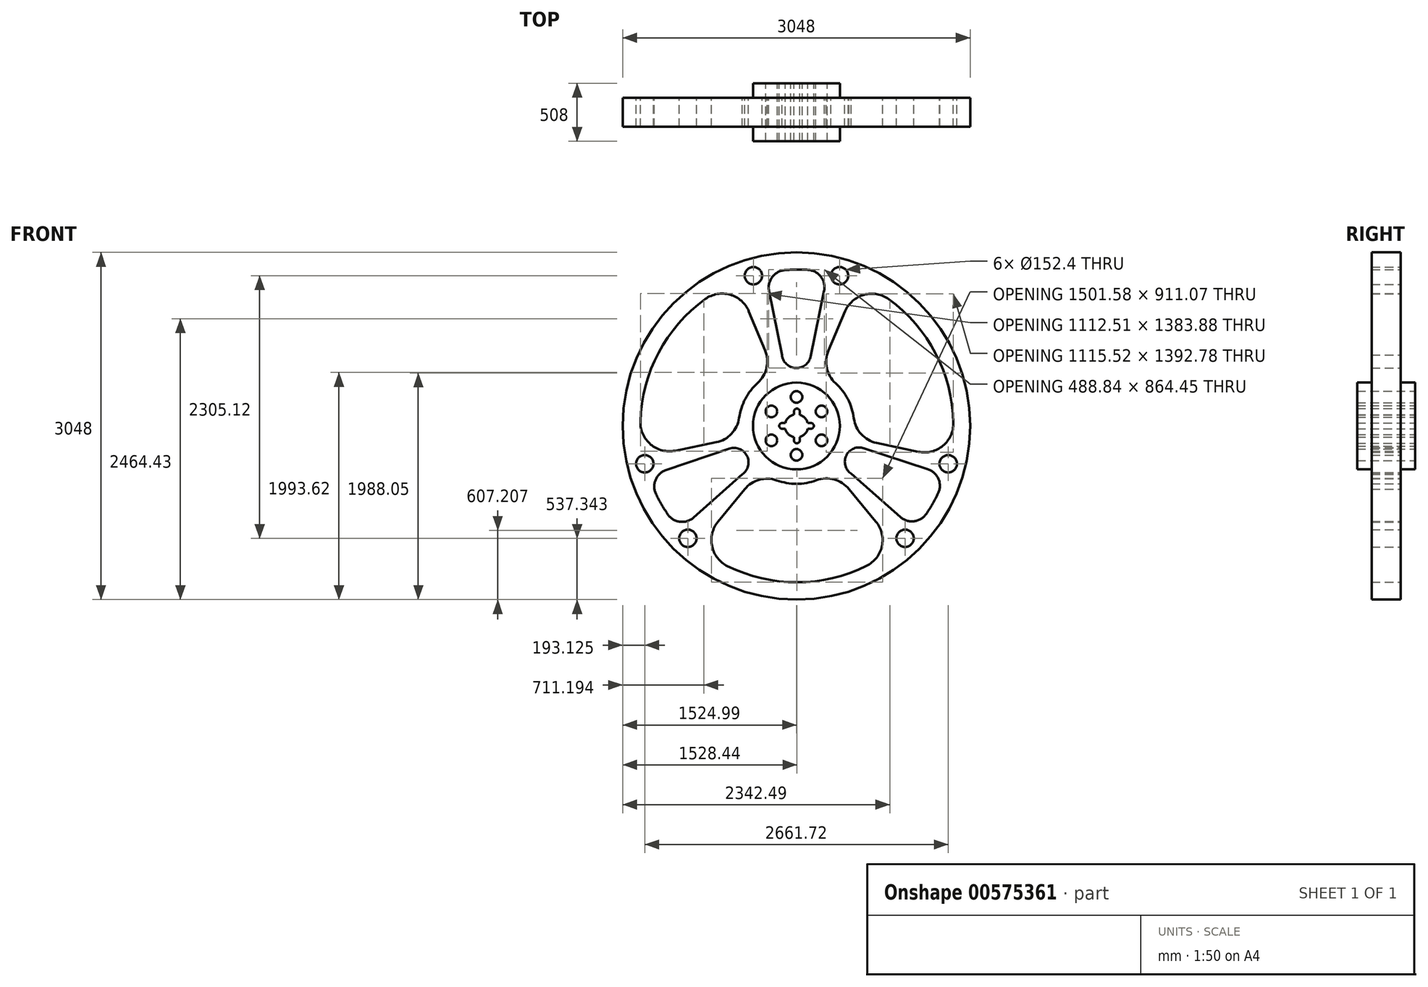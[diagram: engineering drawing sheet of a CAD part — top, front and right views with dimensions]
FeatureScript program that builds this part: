
annotation { "Feature Type Name" : "Feature", "Feature Type Description" : "" }
export const myFeature = defineFeature(function(context is Context, id is Id, definition is map)
    precondition{}
    {
        {
            var Q0;
            Q0=qCreatedBy(makeId("Front.planeOp"),FACE);
            var sketch = newSketch(context, id + "F0", { "sketchPlane" : qUnion([Q0])});
            skCircle(sketch, "E0", {"center": v(0, 0) * mm, "radius": 1524 * mm});
            skArc(sketch, "E1", {"start": v(503.66, 66.28) * mm, "mid": v(450.5, 234.77) * mm, "end": v(342.84, 374.86) * mm});
            skCircle(sketch, "E2", {"center": v(-378.06, 1318.47) * mm, "radius": 76.2 * mm});
            skCircle(sketch, "E3", {"center": v(378.06, 1318.47) * mm, "radius": 76.2 * mm});
            skCircle(sketch, "E4.1.0", {"center": v(-952.81, -986.64) * mm, "radius": 76.2 * mm});
            skCircle(sketch, "E4.1.1", {"center": v(-1330.88, -331.8) * mm, "radius": 76.2 * mm});
            skCircle(sketch, "E4.2.0", {"center": v(1330.84, -331.83) * mm, "radius": 76.2 * mm});
            skCircle(sketch, "E4.2.1", {"center": v(952.78, -986.66) * mm, "radius": 76.2 * mm});
            skPoint(sketch, "E4.center", {"position": v(-0.01, 0) * mm});
            skLineSegment(sketch, "E5", {"start": v(-588.68, -199.42) * mm, "end": v(-1143.8, -387.47) * mm});
            skLineSegment(sketch, "E6", {"start": v(-451.96, -402.88) * mm, "end": v(-901.6, -803.7) * mm});
            skLineSegment(sketch, "E7", {"start": v(457.22, -400.88) * mm, "end": v(912.5, -800.05) * mm});
            skLineSegment(sketch, "E8", {"start": v(590.9, -194.77) * mm, "end": v(1152.91, -380.02) * mm});
            skLineSegment(sketch, "E9", {"start": v(702.79, -149.05) * mm, "end": v(1069.6, -226.85) * mm});
            skLineSegment(sketch, "E10", {"start": v(460.78, -555.07) * mm, "end": v(696.7, -839.27) * mm});
            skLineSegment(sketch, "E11", {"start": v(-455.06, -555.92) * mm, "end": v(-688.92, -841.6) * mm});
            skLineSegment(sketch, "E12", {"start": v(-240.4, 1185.5) * mm, "end": v(-120.85, 595.95) * mm});
            skLineSegment(sketch, "E13", {"start": v(242.35, 1187.25) * mm, "end": v(124.43, 609.6) * mm});
            skLineSegment(sketch, "E14", {"start": v(426.43, 1005.85) * mm, "end": v(280.41, 661.44) * mm});
            skLineSegment(sketch, "E15", {"start": v(-275.36, 663.56) * mm, "end": v(-417.14, 1005.24) * mm});
            skLineSegment(sketch, "E16", {"start": v(-703.9, -143.68) * mm, "end": v(-1064.36, -217.26) * mm});
            skArc(sketch, "E17.trimOffspring", {"start": v(-173.09, -477.6) * mm, "mid": v(0.96, -508) * mm, "end": v(174.88, -476.95) * mm});
            skArc(sketch, "E18.trimOffspring", {"start": v(-339.97, 377.47) * mm, "mid": v(-448.7, 238.2) * mm, "end": v(-503.14, 70.12) * mm});
            skArc(sketch, "E19.trimOffspring", {"start": v(-800.46, 1113.8) * mm, "mid": v(-1210.3, 642.6) * mm, "end": v(-1369.06, 38.62) * mm});
            skArc(sketch, "E20.trimOffspring", {"start": v(102.94, 1369.8) * mm, "mid": v(-0.64, 1372.63) * mm, "end": v(-104.13, 1367.63) * mm});
            skArc(sketch, "E21.trimOffspring", {"start": v(1376.26, 26.37) * mm, "mid": v(1220.64, 636.09) * mm, "end": v(809.37, 1112.36) * mm});
            skArc(sketch, "E22.trimOffspring", {"start": v(1139.02, -771.13) * mm, "mid": v(1194.32, -682.72) * mm, "end": v(1242.76, -590.36) * mm});
            skArc(sketch, "E23.trimOffspring", {"start": v(-604.91, -1230.2) * mm, "mid": v(4.81, -1372.33) * mm, "end": v(614.25, -1228.99) * mm});
            skArc(sketch, "E24.trimOffspring", {"start": v(-1232.03, -598.3) * mm, "mid": v(-1183.69, -689.17) * mm, "end": v(-1128.67, -776.16) * mm});
            skArc(sketch, "E25", {"start": v(-126.51, 623.9) * mm, "mid": v(-7.22, 508.2) * mm, "end": v(124.43, 609.6) * mm});
            skArc(sketch, "E26", {"start": v(590.9, -194.77) * mm, "mid": v(437.5, -258.68) * mm, "end": v(478.67, -419.68) * mm});
            skArc(sketch, "E27", {"start": v(-476.28, -424.56) * mm, "mid": v(-434.3, -262.98) * mm, "end": v(-588.68, -199.42) * mm});
            skArc(sketch, "E28", {"start": v(-688.92, -841.6) * mm, "mid": v(-740.64, -1056.15) * mm, "end": v(-604.91, -1230.2) * mm});
            skArc(sketch, "E29", {"start": v(614.25, -1228.99) * mm, "mid": v(749.76, -1054.08) * mm, "end": v(696.7, -839.27) * mm});
            skArc(sketch, "E30.trimOffspring", {"start": v(-173.09, -477.6) * mm, "mid": v(-326.49, -472.07) * mm, "end": v(-455.06, -555.92) * mm});
            skArc(sketch, "E31.trimOffspring", {"start": v(460.78, -555.07) * mm, "mid": v(330.4, -469.99) * mm, "end": v(174.88, -476.95) * mm});
            skArc(sketch, "E32", {"start": v(-1369.06, 38.62) * mm, "mid": v(-1278.5, -162.9) * mm, "end": v(-1064.36, -217.26) * mm});
            skArc(sketch, "E33", {"start": v(-417.14, 1005.24) * mm, "mid": v(-582.53, 1152.27) * mm, "end": v(-800.46, 1113.8) * mm});
            skArc(sketch, "E34", {"start": v(-339.97, 377.47) * mm, "mid": v(-262.2, 510.24) * mm, "end": v(-275.36, 663.56) * mm});
            skArc(sketch, "E35", {"start": v(280.41, 661.44) * mm, "mid": v(266.09, 508.23) * mm, "end": v(342.84, 374.86) * mm});
            skArc(sketch, "E36", {"start": v(809.37, 1112.36) * mm, "mid": v(592.22, 1151.42) * mm, "end": v(426.43, 1005.85) * mm});
            skArc(sketch, "E37", {"start": v(503.66, 66.28) * mm, "mid": v(569, -73.03) * mm, "end": v(702.79, -149.05) * mm});
            skArc(sketch, "E38", {"start": v(-703.9, -143.68) * mm, "mid": v(-569.54, -68.69) * mm, "end": v(-503.14, 70.12) * mm});
            skArc(sketch, "E39", {"start": v(1069.6, -226.85) * mm, "mid": v(1284.03, -174.23) * mm, "end": v(1376.26, 26.37) * mm});
            skArc(sketch, "E40", {"start": v(-104.13, 1367.63) * mm, "mid": v(-213.06, 1307.1) * mm, "end": v(-240.4, 1185.5) * mm});
            skArc(sketch, "E41", {"start": v(242.35, 1187.25) * mm, "mid": v(214.15, 1310.22) * mm, "end": v(102.94, 1369.8) * mm});
            skArc(sketch, "E42", {"start": v(-1143.8, -387.47) * mm, "mid": v(-1235.48, -472.97) * mm, "end": v(-1232.03, -598.3) * mm});
            skArc(sketch, "E43", {"start": v(-1128.67, -776.16) * mm, "mid": v(-1021.36, -841.22) * mm, "end": v(-901.6, -803.7) * mm});
            skArc(sketch, "E44", {"start": v(912.5, -800.05) * mm, "mid": v(1032.28, -836.63) * mm, "end": v(1139.02, -771.13) * mm});
            skArc(sketch, "E45", {"start": v(1242.76, -590.36) * mm, "mid": v(1245.35, -464.9) * mm, "end": v(1152.91, -380.02) * mm});
            skCircle(sketch, "E46", {"center": v(0, 0) * mm, "radius": 381 * mm});
            skArc(sketch, "E47", {"start": v(3.46, -152.36) * mm, "mid": v(4.15, -152.34) * mm, "end": v(4.84, -152.32) * mm});
            skArc(sketch, "E48", {"start": v(98.2, 26.04) * mm, "mid": v(72.86, 70.8) * mm, "end": v(28.86, 97.41) * mm});
            skLineSegment(sketch, "E49", {"start": v(-152.4, 0) * mm, "end": v(-151.18, 0) * mm});
            skCircle(sketch, "E50", {"center": v(0, 254) * mm, "radius": 50.8 * mm});
            skCircle(sketch, "E51.1.0", {"center": v(-219.97, 127) * mm, "radius": 50.8 * mm});
            skCircle(sketch, "E51.2.0", {"center": v(-219.97, -127) * mm, "radius": 50.8 * mm});
            skCircle(sketch, "E51.3.0", {"center": v(0, -254) * mm, "radius": 50.8 * mm});
            skCircle(sketch, "E51.4.0", {"center": v(219.97, -127) * mm, "radius": 50.8 * mm});
            skCircle(sketch, "E51.5.0", {"center": v(219.97, 127) * mm, "radius": 50.8 * mm});
            skPoint(sketch, "E52.orphan", {"position": v(-381, 0) * mm});
            skLineSegment(sketch, "E53.trimOffspring", {"start": v(0, 254) * mm, "end": v(0, 381) * mm});
            skLineSegment(sketch, "E54.trimOffspring", {"start": v(-101.61, 0) * mm, "end": v(-100.38, 0) * mm});
            skPoint(sketch, "E55.start.orphan", {"position": v(0, -381) * mm});
            skArc(sketch, "E56", {"start": v(127, -24.76) * mm, "mid": v(152.4, 0.64) * mm, "end": v(127, 26.04) * mm});
            skLineSegment(sketch, "E57", {"start": v(127, 26.04) * mm, "end": v(98.2, 26.04) * mm});
            skLineSegment(sketch, "E58", {"start": v(127, -24.76) * mm, "end": v(98.53, -24.76) * mm});
            skPoint(sketch, "E59.start.orphan", {"position": v(152.4, 0.71) * mm});
            skArc(sketch, "E60", {"start": v(28.86, 126.96) * mm, "mid": v(3.46, 152.36) * mm, "end": v(-21.94, 126.96) * mm});
            skArc(sketch, "E61", {"start": v(-125.79, 26.11) * mm, "mid": v(-151.19, 0.71) * mm, "end": v(-125.79, -24.69) * mm});
            skArc(sketch, "E62", {"start": v(-21.94, -126.96) * mm, "mid": v(3.46, -152.36) * mm, "end": v(28.86, -126.96) * mm});
            skLineSegment(sketch, "E63", {"start": v(-125.79, -24.69) * mm, "end": v(-98.57, -24.69) * mm});
            skLineSegment(sketch, "E64", {"start": v(-125.79, 26.11) * mm, "end": v(-98.2, 26.11) * mm});
            skLineSegment(sketch, "E65", {"start": v(-21.94, 126.96) * mm, "end": v(-21.94, 99.2) * mm});
            skLineSegment(sketch, "E66", {"start": v(28.86, 126.96) * mm, "end": v(28.86, 97.41) * mm});
            skLineSegment(sketch, "E67", {"start": v(-21.94, -126.96) * mm, "end": v(-21.94, -99.2) * mm});
            skLineSegment(sketch, "E68", {"start": v(28.86, -126.96) * mm, "end": v(28.86, -97.41) * mm});
            skArc(sketch, "E69.trimOffspring", {"start": v(28.86, -97.41) * mm, "mid": v(73.32, -70.32) * mm, "end": v(98.53, -24.76) * mm});
            skPoint(sketch, "E70.start.orphan", {"position": v(3.46, -152.36) * mm});
            skArc(sketch, "E71.trimOffspring", {"start": v(-98.57, -24.69) * mm, "mid": v(-70.85, -72.84) * mm, "end": v(-21.94, -99.2) * mm});
            skArc(sketch, "E72.trimOffspring", {"start": v(-21.94, 99.2) * mm, "mid": v(-70.32, 73.35) * mm, "end": v(-98.2, 26.11) * mm});
            skPoint(sketch, "E73.start.orphan", {"position": v(3.46, 152.36) * mm});
            skArc(sketch, "E74.trimOffspring", {"start": v(4.84, 152.32) * mm, "mid": v(4.15, 152.34) * mm, "end": v(3.46, 152.36) * mm});
            skArc(sketch, "E75.trimOffspring", {"start": v(152.4, 0.64) * mm, "mid": v(152.4, 0.77) * mm, "end": v(152.4, 0.9) * mm});
            skSolve(sketch);
        }
        {
            var Q0;
            Q0=makeQuery(id+"F0.imprint","IMPRINT",FACE,{"disambiguationData":[TD([[makeQuery(id+"F0.imprint","IMPRINT",EDGE,{"derivedFrom":sQuery(id+"F0.wireOp",EDGE,"E0")}),1.0]])]});
            extrude(context, id + "F1", {"entities" : qUnion([Q0]), "depth" : 254 * mm, "offsetDistance" : 25.4 * mm, "symmetric" : true});
        }
        {
            var Q0;
            Q0=makeQuery(id+"F0.imprint","IMPRINT",FACE,{"disambiguationData":[TD([[makeQuery(id+"F0.imprint","IMPRINT",EDGE,{"derivedFrom":sQuery(id+"F0.wireOp",EDGE,"E46")}),1.0]])]});
            extrude(context, id + "F2", {"entities" : qUnion([Q0]), "operationType" : NewBodyOperationType.ADD, "depth" : 508 * mm, "offsetDistance" : 25.4 * mm, "symmetric" : true});
        }
    });
